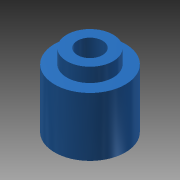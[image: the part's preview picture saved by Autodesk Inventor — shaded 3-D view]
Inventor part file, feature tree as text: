
AUTODESK INVENTOR PART (.ipt)
format: ipt  version: 2013 SP2 (Build 170200200, 200)  size: 89,088 bytes
history: native  units: mm
features: extrude x2, sketch x2
ambient origin geometry x8: Origin, YZ Plane, XZ Plane, XY Plane, X Axis, Y Axis, Z Axis, Center Point
bodies: Solid1 (feature_tree)
feature tree (4):
  extrude  "Extrusion1"  Depth=9.0mm
  extrude  "Extrusion2"  Depth=5.9mm
  sketch  "Sketch1"  dims[d0=3.2mm d1=9.0mm]
  sketch  "Sketch2"  dims[d2=7.5mm d3=0.0mm d4=5.9mm d5=1.8mm d6=0.0mm]
